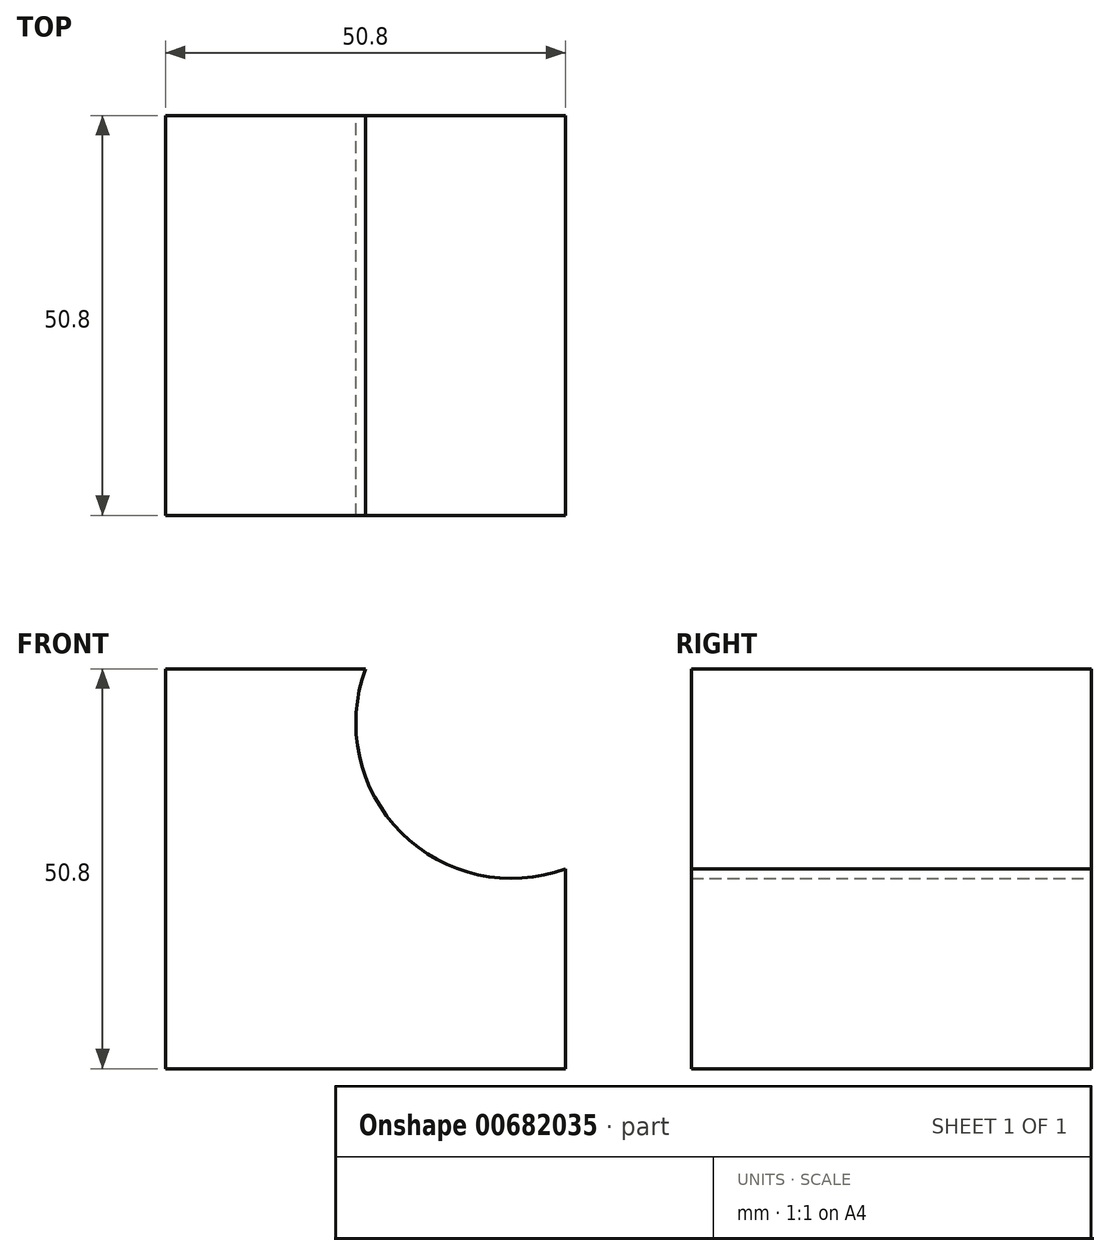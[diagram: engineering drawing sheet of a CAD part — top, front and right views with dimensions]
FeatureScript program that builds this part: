
annotation { "Feature Type Name" : "Feature", "Feature Type Description" : "" }
export const myFeature = defineFeature(function(context is Context, id is Id, definition is map)
    precondition{}
    {
        {
            var Q0;
            Q0=qCreatedBy(makeId("Front.planeOp"),FACE);
            var sketch = newSketch(context, id + "F0", { "sketchPlane" : qUnion([Q0])});
            skLineSegment(sketch, "E0", {"start": v(-57.76, 48.99) * mm, "end": v(-57.76, -1.81) * mm});
            skLineSegment(sketch, "E1", {"start": v(-57.76, -1.81) * mm, "end": v(-6.96, -1.81) * mm});
            skLineSegment(sketch, "E2", {"start": v(-57.76, 48.99) * mm, "end": v(-32.36, 48.99) * mm});
            skLineSegment(sketch, "E3", {"start": v(-6.96, -1.81) * mm, "end": v(-6.96, 23.59) * mm});
            skArc(sketch, "E4", {"start": v(-32.36, 48.99) * mm, "mid": v(-27.8, 28.14) * mm, "end": v(-6.96, 23.59) * mm});
            skSolve(sketch);
        }
        {
            var Q0;
            Q0 = qSketchRegion(id + "F0", true);
            extrude(context, id + "F1", {"entities" : qUnion([Q0]), "depth" : 50.8 * mm, "offsetDistance" : 25.4 * mm});
        }
    });
